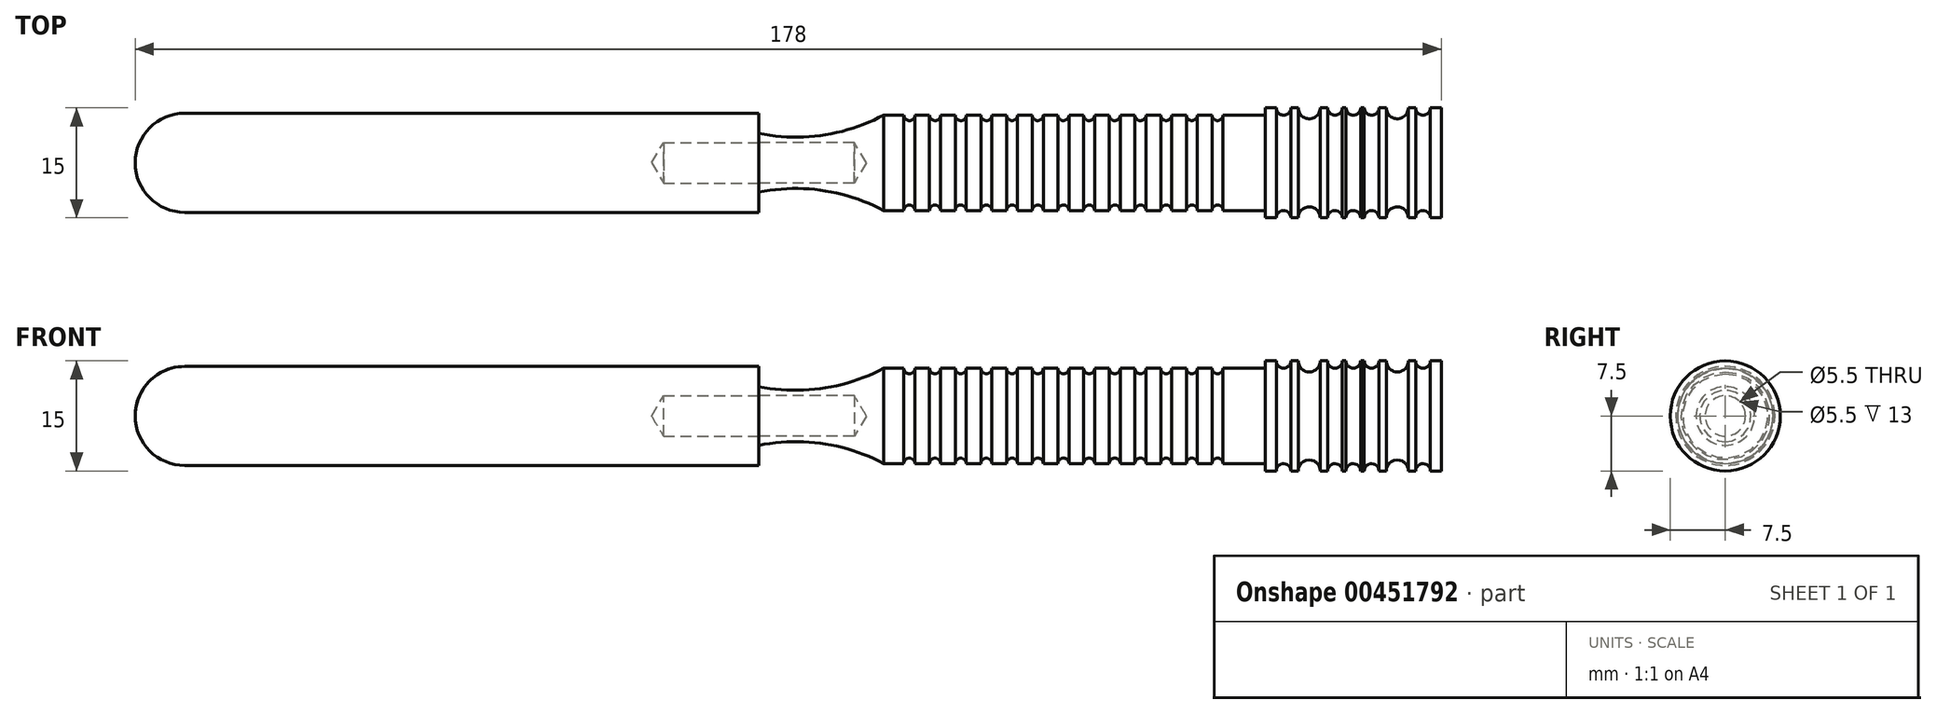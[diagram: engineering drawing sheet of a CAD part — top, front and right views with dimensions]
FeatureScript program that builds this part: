
annotation { "Feature Type Name" : "Feature", "Feature Type Description" : "" }
export const myFeature = defineFeature(function(context is Context, id is Id, definition is map)
    precondition{}
    {
        {
            var Q0;
            Q0=qCreatedBy(makeId("Front.planeOp"),FACE);
            var sketch = newSketch(context, id + "F0", { "sketchPlane" : qUnion([Q0])});
            skLineSegment(sketch, "E0", {"start": v(0, 0) * mm, "end": v(0, 4) * mm});
            skArc(sketch, "E1", {"start": v(0, 4) * mm, "mid": v(8.72, 3.77) * mm, "end": v(17, 6.5) * mm});
            skLineSegment(sketch, "E2", {"start": v(17, 6.5) * mm, "end": v(69, 6.5) * mm});
            skLineSegment(sketch, "E3", {"start": v(69, 6.5) * mm, "end": v(69, 7.5) * mm});
            skLineSegment(sketch, "E4", {"start": v(69, 7.5) * mm, "end": v(93, 7.5) * mm});
            skLineSegment(sketch, "E5", {"start": v(93, 7.5) * mm, "end": v(93, 0) * mm});
            skLineSegment(sketch, "E6", {"start": v(93, 0) * mm, "end": v(0, 0) * mm});
            skLineSegment(sketch, "E7.MirrorCS", {"start": v(0, 0) * mm, "end": v(0, -4) * mm});
            skArc(sketch, "E8.MirrorC", {"start": v(0, -4) * mm, "mid": v(8.72, -3.77) * mm, "end": v(17, -6.5) * mm});
            skLineSegment(sketch, "E9.MirrorCS", {"start": v(69, -6.5) * mm, "end": v(69, -7.5) * mm});
            skLineSegment(sketch, "E10.MirrorCS", {"start": v(69, -7.5) * mm, "end": v(93, -7.5) * mm});
            skLineSegment(sketch, "E11.MirrorCS", {"start": v(17, -6.5) * mm, "end": v(69, -6.5) * mm});
            skLineSegment(sketch, "E12.MirrorCS", {"start": v(93, -7.5) * mm, "end": v(93, 0) * mm});
            skSolve(sketch);
        }
        {
            var Q0;
            Q0=makeQuery(id+"F0.imprint","IMPRINT",FACE,{"disambiguationData":[TD([[makeQuery(id+"F0.imprint","IMPRINT",EDGE,{"derivedFrom":sQuery(id+"F0.wireOp",EDGE,"E6")}),1.0]])]});
            var Q1;
            Q1=sQuery(id+"F0.wireOp",EDGE,"E6");
            revolve(context, id + "F1", {"entities" : qUnion([Q0]), "axis" : qUnion([Q1]), "revolveType" : RevolveType.FULL});
        }
        {
            var Q0;
            Q0=qCreatedBy(makeId("Front.planeOp"),FACE);
            var sketch = newSketch(context, id + "F2", { "sketchPlane" : qUnion([Q0])});
            skCircle(sketch, "E13", {"center": v(20.5, 6.5) * mm, "radius": 0.75 * mm});
            skLineSegment(sketch, "E14", {"start": v(17, 6.5) * mm, "end": v(69, 6.5) * mm, "construction": true});
            skLineSegment(sketch, "E15", {"start": v(69, 7.5) * mm, "end": v(93, 7.5) * mm, "construction": true});
            skCircle(sketch, "E16.1.0.0", {"center": v(24, 6.5) * mm, "radius": 0.75 * mm});
            skCircle(sketch, "E16.2.0.0", {"center": v(27.5, 6.5) * mm, "radius": 0.75 * mm});
            skCircle(sketch, "E16.3.0.0", {"center": v(31, 6.5) * mm, "radius": 0.75 * mm});
            skCircle(sketch, "E16.4.0.0", {"center": v(34.5, 6.5) * mm, "radius": 0.75 * mm});
            skCircle(sketch, "E16.5.0.0", {"center": v(38, 6.5) * mm, "radius": 0.75 * mm});
            skCircle(sketch, "E16.6.0.0", {"center": v(41.5, 6.5) * mm, "radius": 0.75 * mm});
            skCircle(sketch, "E16.7.0.0", {"center": v(45, 6.5) * mm, "radius": 0.75 * mm});
            skCircle(sketch, "E16.8.0.0", {"center": v(48.5, 6.5) * mm, "radius": 0.75 * mm});
            skCircle(sketch, "E16.9.0.0", {"center": v(52, 6.5) * mm, "radius": 0.75 * mm});
            skCircle(sketch, "E16.10.0.0", {"center": v(55.5, 6.5) * mm, "radius": 0.75 * mm});
            skCircle(sketch, "E16.11.0.0", {"center": v(59, 6.5) * mm, "radius": 0.75 * mm});
            skCircle(sketch, "E16.12.0.0", {"center": v(62.5, 6.5) * mm, "radius": 0.75 * mm});
            skLineSegment(sketch, "E16.direction1", {"start": v(20.5, 6.5) * mm, "end": v(24, 6.5) * mm, "construction": true});
            skCircle(sketch, "E17", {"center": v(71.5, 7.5) * mm, "radius": 1 * mm});
            skCircle(sketch, "E18", {"center": v(75, 7.5) * mm, "radius": 1.5 * mm});
            skCircle(sketch, "E19", {"center": v(78.5, 7.5) * mm, "radius": 1 * mm});
            skCircle(sketch, "E20", {"center": v(81, 7.5) * mm, "radius": 1 * mm});
            skCircle(sketch, "E21", {"center": v(83.5, 7.5) * mm, "radius": 1 * mm});
            skCircle(sketch, "E22", {"center": v(87, 7.5) * mm, "radius": 1.5 * mm});
            skCircle(sketch, "E23", {"center": v(90.5, 7.5) * mm, "radius": 1 * mm});
            skSolve(sketch);
        }
        {
            var Q0;
            Q0=makeQuery(id+"F2.imprint","IMPRINT",FACE,{"disambiguationData":[TD([[makeQuery(id+"F2.imprint","IMPRINT",EDGE,{"derivedFrom":sQuery(id+"F2.wireOp",EDGE,"E13")}),1.0]])]});
            var Q1;
            Q1=makeQuery(id+"F2.imprint","IMPRINT",FACE,{"disambiguationData":[TD([[makeQuery(id+"F2.imprint","IMPRINT",EDGE,{"derivedFrom":sQuery(id+"F2.wireOp",EDGE,"E16.1.0.0")}),1.0]])]});
            var Q2;
            Q2=makeQuery(id+"F2.imprint","IMPRINT",FACE,{"disambiguationData":[TD([[makeQuery(id+"F2.imprint","IMPRINT",EDGE,{"derivedFrom":sQuery(id+"F2.wireOp",EDGE,"E16.2.0.0")}),1.0]])]});
            var Q3;
            Q3=makeQuery(id+"F2.imprint","IMPRINT",FACE,{"disambiguationData":[TD([[makeQuery(id+"F2.imprint","IMPRINT",EDGE,{"derivedFrom":sQuery(id+"F2.wireOp",EDGE,"E16.3.0.0")}),1.0]])]});
            var Q4;
            Q4=makeQuery(id+"F2.imprint","IMPRINT",FACE,{"disambiguationData":[TD([[makeQuery(id+"F2.imprint","IMPRINT",EDGE,{"derivedFrom":sQuery(id+"F2.wireOp",EDGE,"E16.4.0.0")}),1.0]])]});
            var Q5;
            Q5=makeQuery(id+"F2.imprint","IMPRINT",FACE,{"disambiguationData":[TD([[makeQuery(id+"F2.imprint","IMPRINT",EDGE,{"derivedFrom":sQuery(id+"F2.wireOp",EDGE,"E16.5.0.0")}),1.0]])]});
            var Q6;
            Q6=makeQuery(id+"F2.imprint","IMPRINT",FACE,{"disambiguationData":[TD([[makeQuery(id+"F2.imprint","IMPRINT",EDGE,{"derivedFrom":sQuery(id+"F2.wireOp",EDGE,"E16.6.0.0")}),1.0]])]});
            var Q7;
            Q7=makeQuery(id+"F2.imprint","IMPRINT",FACE,{"disambiguationData":[TD([[makeQuery(id+"F2.imprint","IMPRINT",EDGE,{"derivedFrom":sQuery(id+"F2.wireOp",EDGE,"E16.7.0.0")}),1.0]])]});
            var Q8;
            Q8=makeQuery(id+"F2.imprint","IMPRINT",FACE,{"disambiguationData":[TD([[makeQuery(id+"F2.imprint","IMPRINT",EDGE,{"derivedFrom":sQuery(id+"F2.wireOp",EDGE,"E16.8.0.0")}),1.0]])]});
            var Q9;
            Q9=makeQuery(id+"F2.imprint","IMPRINT",FACE,{"disambiguationData":[TD([[makeQuery(id+"F2.imprint","IMPRINT",EDGE,{"derivedFrom":sQuery(id+"F2.wireOp",EDGE,"E16.9.0.0")}),1.0]])]});
            var Q10;
            Q10=makeQuery(id+"F2.imprint","IMPRINT",FACE,{"disambiguationData":[TD([[makeQuery(id+"F2.imprint","IMPRINT",EDGE,{"derivedFrom":sQuery(id+"F2.wireOp",EDGE,"E16.10.0.0")}),1.0]])]});
            var Q11;
            Q11=makeQuery(id+"F2.imprint","IMPRINT",FACE,{"disambiguationData":[TD([[makeQuery(id+"F2.imprint","IMPRINT",EDGE,{"derivedFrom":sQuery(id+"F2.wireOp",EDGE,"E16.11.0.0")}),1.0]])]});
            var Q12;
            Q12=makeQuery(id+"F2.imprint","IMPRINT",FACE,{"disambiguationData":[TD([[makeQuery(id+"F2.imprint","IMPRINT",EDGE,{"derivedFrom":sQuery(id+"F2.wireOp",EDGE,"E16.12.0.0")}),1.0]])]});
            var Q13;
            Q13=makeQuery(id+"F2.imprint","IMPRINT",FACE,{"disambiguationData":[TD([[makeQuery(id+"F2.imprint","IMPRINT",EDGE,{"derivedFrom":sQuery(id+"F2.wireOp",EDGE,"E17")}),1.0]])]});
            var Q14;
            Q14=makeQuery(id+"F2.imprint","IMPRINT",FACE,{"disambiguationData":[TD([[makeQuery(id+"F2.imprint","IMPRINT",EDGE,{"derivedFrom":sQuery(id+"F2.wireOp",EDGE,"E18")}),1.0]])]});
            var Q15;
            Q15=makeQuery(id+"F2.imprint","IMPRINT",FACE,{"disambiguationData":[TD([[makeQuery(id+"F2.imprint","IMPRINT",EDGE,{"derivedFrom":sQuery(id+"F2.wireOp",EDGE,"E19")}),1.0]])]});
            var Q16;
            Q16=makeQuery(id+"F2.imprint","IMPRINT",FACE,{"disambiguationData":[TD([[makeQuery(id+"F2.imprint","IMPRINT",EDGE,{"derivedFrom":sQuery(id+"F2.wireOp",EDGE,"E20")}),1.0]])]});
            var Q17;
            Q17=makeQuery(id+"F2.imprint","IMPRINT",FACE,{"disambiguationData":[TD([[makeQuery(id+"F2.imprint","IMPRINT",EDGE,{"derivedFrom":sQuery(id+"F2.wireOp",EDGE,"E21")}),1.0]])]});
            var Q18;
            Q18=makeQuery(id+"F2.imprint","IMPRINT",FACE,{"disambiguationData":[TD([[makeQuery(id+"F2.imprint","IMPRINT",EDGE,{"derivedFrom":sQuery(id+"F2.wireOp",EDGE,"E22")}),1.0]])]});
            var Q19;
            Q19=makeQuery(id+"F2.imprint","IMPRINT",FACE,{"disambiguationData":[TD([[makeQuery(id+"F2.imprint","IMPRINT",EDGE,{"derivedFrom":sQuery(id+"F2.wireOp",EDGE,"E23")}),1.0]])]});
            var Q20;
            Q20=sQuery(id+"F0.wireOp",EDGE,"E6");
            revolve(context, id + "F3", {"operationType" : NewBodyOperationType.REMOVE, "entities" : qUnion([Q0, Q1, Q2, Q3, Q4, Q5, Q6, Q7, Q8, Q9, Q10, Q11, Q12, Q13, Q14, Q15, Q16, Q17, Q18, Q19]), "axis" : qUnion([Q20]), "revolveType" : RevolveType.FULL, "oppositeDirection" : true});
        }
        {
            var Q0;
            Q0=makeQuery(id+"F1.opRevolve","SWEPT_FACE",FACE,{"disambiguationData":[OSD([sQuery(id+"F0.wireOp",EDGE,"E7.MirrorCS")])]});
            var sketch = newSketch(context, id + "F4", { "sketchPlane" : qUnion([Q0])});
            skPoint(sketch, "E24", {"position": v(0, 0) * mm});
            skSolve(sketch);
        }
        {
            var Q0;
            Q0=sQuery(id+"F4.wireOp",VERTEX,"E24");
            var Q1;
            Q1=makeQuery(id+"F1.opRevolve","SWEPT_BODY",BODY,{"disambiguationData":[OSD([sQuery(id+"F0.wireOp",EDGE,"E6"),sQuery(id+"F0.wireOp",EDGE,"E7.MirrorCS"),sQuery(id+"F0.wireOp",EDGE,"E8.MirrorC"),sQuery(id+"F0.wireOp",EDGE,"E9.MirrorCS"),sQuery(id+"F0.wireOp",EDGE,"E10.MirrorCS"),sQuery(id+"F0.wireOp",EDGE,"E11.MirrorCS"),sQuery(id+"F0.wireOp",EDGE,"E12.MirrorCS")])]});
            hole(context, id + "F5", {"style" : HoleStyle.SIMPLE, "endStyle" : HoleEndStyle.BLIND, "standardTappedOrClearance" : lookupTablePath({ "standard" : "ISO", "fit" : "Normal", "size" : "M5", "type" : "Clearance" }), "standardBlindInLast" : lookupTablePath({ "fit" : "Standard", "standard" : "ISO", "size" : "M5", "type" : "Clearance" }), "holeDiameter" : 5.5 * mm, "holeDepth" : 13 * mm, "tappedDepth" : 12 * mm, "tapClearance" : 3, "startFromSketch" : true, "locations" : qUnion([Q0]), "scope" : qUnion([Q1])});
        }
        {
            var Q0;
            Q0=qCreatedBy(makeId("Front.planeOp"),FACE);
            var sketch = newSketch(context, id + "F6", { "sketchPlane" : qUnion([Q0])});
            skLineSegment(sketch, "E25", {"start": v(0, 0) * mm, "end": v(0, 6.75) * mm});
            skLineSegment(sketch, "E26", {"start": v(0, 6.75) * mm, "end": v(-78.25, 6.75) * mm});
            skLineSegment(sketch, "E27", {"start": v(-85, 0) * mm, "end": v(0, 0) * mm});
            skArc(sketch, "E28", {"start": v(-78.25, 6.75) * mm, "mid": v(-83.02, 4.77) * mm, "end": v(-85, 0) * mm});
            skLineSegment(sketch, "E29.MirrorCS", {"start": v(0, -6.75) * mm, "end": v(-78.25, -6.75) * mm});
            skArc(sketch, "E30.MirrorCS", {"start": v(-78.25, -6.75) * mm, "mid": v(-83.02, -4.77) * mm, "end": v(-85, 0) * mm});
            skLineSegment(sketch, "E31.MirrorCS", {"start": v(0, 0) * mm, "end": v(0, -6.75) * mm});
            skSolve(sketch);
        }
        {
            var Q0;
            Q0=makeQuery(id+"F6.imprint","IMPRINT",FACE,{"disambiguationData":[TD([[makeQuery(id+"F6.imprint","IMPRINT",EDGE,{"derivedFrom":sQuery(id+"F6.wireOp",EDGE,"E25")}),1.0]])]});
            var Q1;
            Q1=sQuery(id+"F6.wireOp",EDGE,"E27");
            revolve(context, id + "F7", {"entities" : qUnion([Q0]), "axis" : qUnion([Q1]), "revolveType" : RevolveType.FULL});
        }
        {
            var Q0;
            Q0=makeQuery(id+"F7.opRevolve","SWEPT_FACE",FACE,{"disambiguationData":[OSD([sQuery(id+"F6.wireOp",EDGE,"E25")])]});
            var sketch = newSketch(context, id + "F8", { "sketchPlane" : qUnion([Q0])});
            skPoint(sketch, "E32", {"position": v(0, 0) * mm});
            skSolve(sketch);
        }
        {
            var Q0;
            Q0=sQuery(id+"F8.wireOp",VERTEX,"E32");
            var Q1;
            Q1=makeQuery(id+"F7.opRevolve","SWEPT_BODY",BODY,{"disambiguationData":[OSD([sQuery(id+"F6.wireOp",EDGE,"E25"),sQuery(id+"F6.wireOp",EDGE,"E26"),sQuery(id+"F6.wireOp",EDGE,"E27"),sQuery(id+"F6.wireOp",EDGE,"E28")])]});
            hole(context, id + "F9", {"style" : HoleStyle.SIMPLE, "endStyle" : HoleEndStyle.BLIND, "standardTappedOrClearance" : lookupTablePath({ "standard" : "ISO", "fit" : "Normal", "size" : "M5", "type" : "Clearance" }), "standardBlindInLast" : lookupTablePath({ "fit" : "Standard", "standard" : "ISO", "size" : "M5", "type" : "Clearance" }), "holeDiameter" : 5.5 * mm, "holeDepth" : 13 * mm, "tappedDepth" : 12 * mm, "tapClearance" : 3, "startFromSketch" : true, "locations" : qUnion([Q0]), "scope" : qUnion([Q1])});
        }
    });
